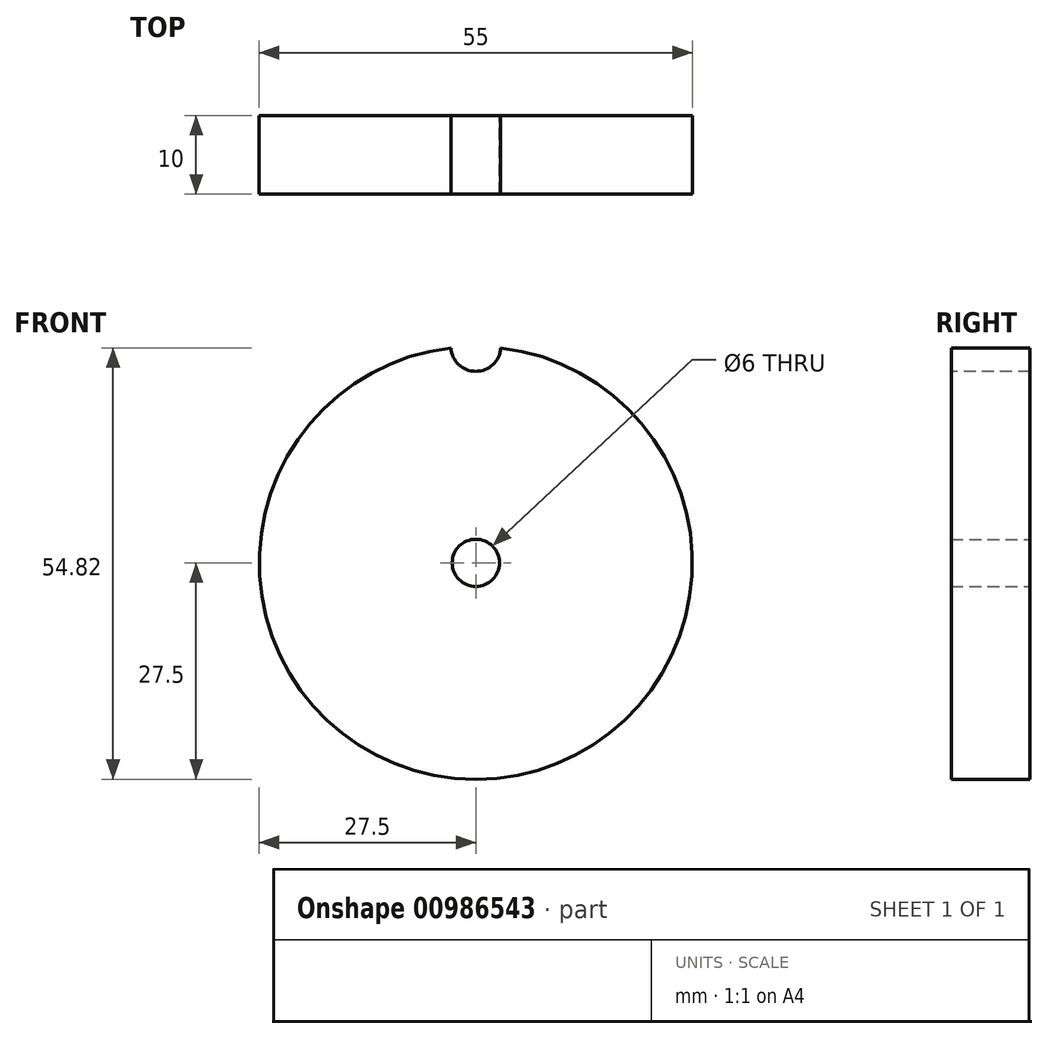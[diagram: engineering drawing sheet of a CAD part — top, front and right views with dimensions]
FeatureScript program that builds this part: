
annotation { "Feature Type Name" : "Feature", "Feature Type Description" : "" }
export const myFeature = defineFeature(function(context is Context, id is Id, definition is map)
    precondition{}
    {
        {
            var Q0;
            Q0=qCreatedBy(makeId("Front.planeOp"),FACE);
            var sketch = newSketch(context, id + "F0", { "sketchPlane" : qUnion([Q0])});
            skCircle(sketch, "E0", {"center": v(0, 0) * mm, "radius": 27.5 * mm});
            skCircle(sketch, "E1", {"center": v(0, 0) * mm, "radius": 3 * mm});
            skSolve(sketch);
        }
        {
            var Q0;
            Q0 = qSketchRegion(id + "F0", true);
            extrude(context, id + "F1", {"entities" : qUnion([Q0]), "depth" : 10 * mm, "offsetDistance" : 25 * mm});
        }
        {
            var Q0;
            Q0=makeQuery(id+"F1.opExtrude","CAP_FACE",FACE,{"disambiguationData":[OSD([sQuery(id+"F0.wireOp",EDGE,"E0")])],"isStart":false});
            var sketch = newSketch(context, id + "F2", { "sketchPlane" : qUnion([Q0])});
            skCircle(sketch, "E2", {"center": v(0, 27.5) * mm, "radius": 3.17 * mm});
            skSolve(sketch);
        }
        {
            var Q0;
            Q0 = qSketchRegion(id + "F2", true);
            extrude(context, id + "F3", {"entities" : qUnion([Q0]), "operationType" : NewBodyOperationType.REMOVE, "endBound" : BoundingType.THROUGH_ALL, "oppositeDirection" : true, "depth" : 25 * mm, "offsetDistance" : 25 * mm});
        }
    });
